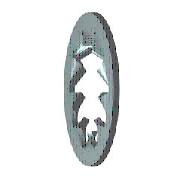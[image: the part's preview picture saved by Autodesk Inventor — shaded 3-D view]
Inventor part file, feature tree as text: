
AUTODESK INVENTOR PART (.ipt)
format: ipt  version: 2015 (Build 190159000, 159)  size: 155,648 bytes
history: native  units: mm (DEFAULTED — no unit token found)
features: sketch x2, extrude x1, pattern_circular x1, plane x1
ambient origin geometry x7: Origin, YZ Plane, XY Plane, X Axis, Y Axis, Z Axis, Center Point
bodies: Solid1 (feature_tree), Body (feature_tree)
feature tree (5):
  extrude  "Cut"  Depth=3.5814mm
  pattern_circular  "Cuts"  [2 undecoded]
  plane  "Work Plane1"
  sketch  "Sketch1"  dims[d0=7.493mm d1=3.5814mm]
  sketch  "Sketch2"  dims[d2=0.5588mm d3=0.0mm d4=5.5372mm d5=15.0deg d6=0.5588mm d7=0.0mm d8=0.107442mm d9=60.0mm d11=360.0deg d12=0.0mm d13=0.0mm d18=0.0mm d19=0.0mm]
note: 2 required parameter values undecoded (feature->parameter linkage not recoverable at this tier; creation-order binding heuristic only, values carry confidence <= 0.55)
